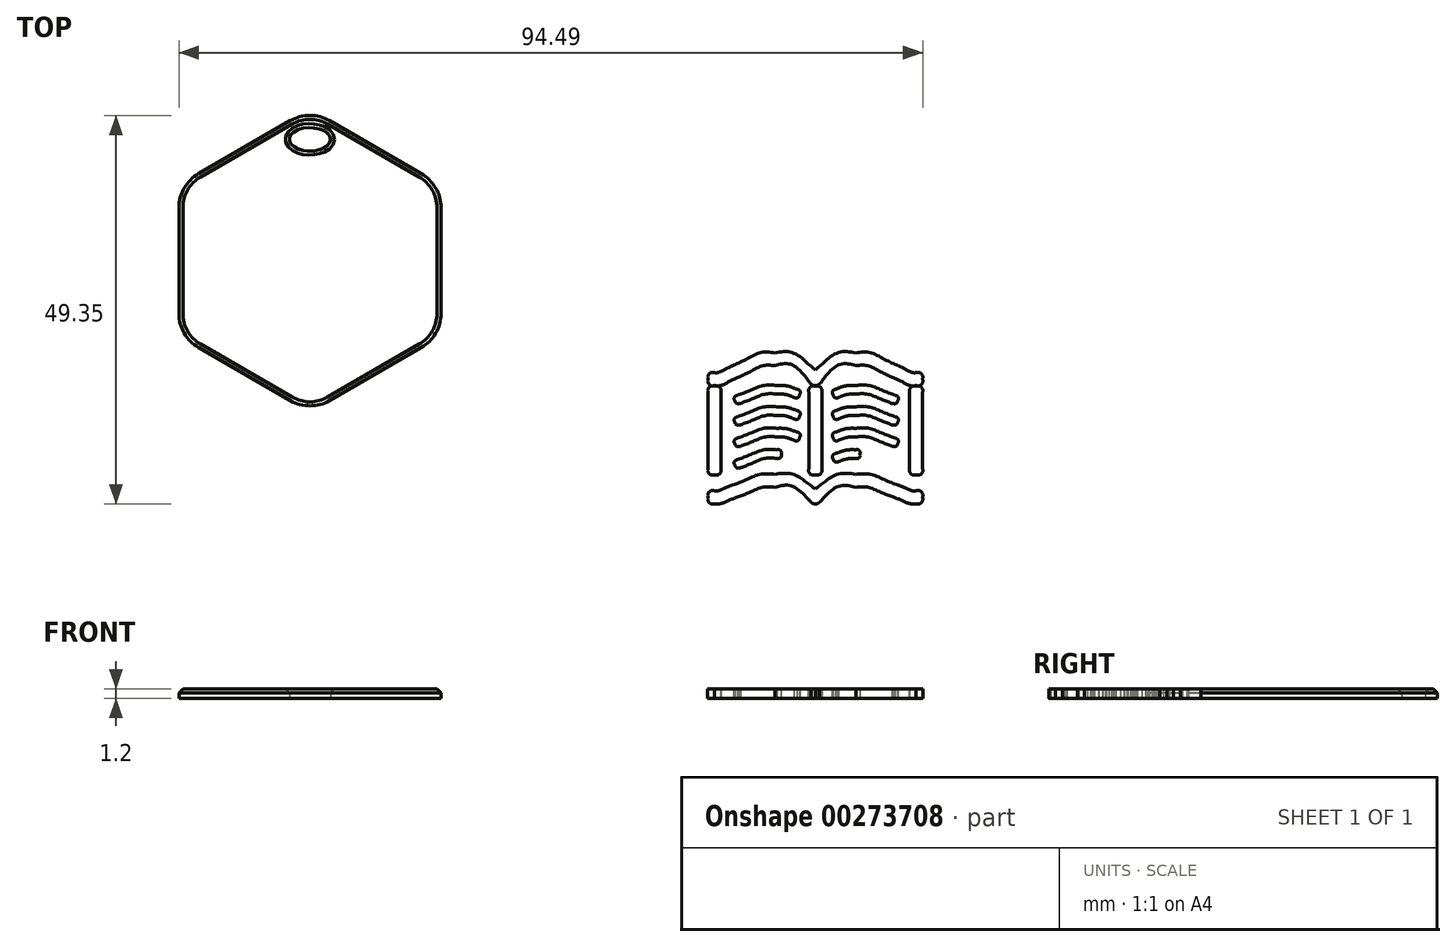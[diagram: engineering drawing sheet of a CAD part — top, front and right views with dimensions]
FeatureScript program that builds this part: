
annotation { "Feature Type Name" : "Feature", "Feature Type Description" : "" }
export const myFeature = defineFeature(function(context is Context, id is Id, definition is map)
    precondition{}
    {
        {
            var Q0;
            Q0=qCreatedBy(makeId("Top.planeOp"),FACE);
            var sketch = newSketch(context, id + "F0", { "sketchPlane" : qUnion([Q0])});
            skCircle(sketch, "E0.cCircle", {"center": v(0, 0) * mm, "radius": 16.64 * mm, "construction": true});
            skLineSegment(sketch, "E0.0", {"start": v(16.64, 6.72) * mm, "end": v(16.64, -6.72) * mm});
            skLineSegment(sketch, "E0.1", {"start": v(14.14, -11.05) * mm, "end": v(2.5, -17.77) * mm});
            skLineSegment(sketch, "E0.2", {"start": v(-2.5, -17.77) * mm, "end": v(-14.14, -11.05) * mm});
            skLineSegment(sketch, "E0.3", {"start": v(-16.64, -6.72) * mm, "end": v(-16.64, 6.72) * mm});
            skLineSegment(sketch, "E0.4", {"start": v(-14.14, 11.05) * mm, "end": v(-2.5, 17.77) * mm});
            skLineSegment(sketch, "E0.5", {"start": v(2.5, 17.77) * mm, "end": v(14.14, 11.05) * mm});
            skPoint(sketch, "E0.0.midPoint", {"position": v(16.64, 0) * mm});
            skPoint(sketch, "E1.visualSharp", {"position": v(-16.64, 9.6) * mm});
            skArc(sketch, "E1.filletArc", {"start": v(-14.14, 11.05) * mm, "mid": v(-15.97, 9.22) * mm, "end": v(-16.64, 6.72) * mm});
            skPoint(sketch, "E2.visualSharp", {"position": v(0, 19.22) * mm});
            skArc(sketch, "E2.filletArc", {"start": v(2.5, 17.77) * mm, "mid": v(0, 18.44) * mm, "end": v(-2.5, 17.77) * mm});
            skPoint(sketch, "E3.visualSharp", {"position": v(16.64, 9.6) * mm});
            skArc(sketch, "E3.filletArc", {"start": v(16.64, 6.72) * mm, "mid": v(15.97, 9.22) * mm, "end": v(14.14, 11.05) * mm});
            skPoint(sketch, "E4.visualSharp", {"position": v(16.64, -9.6) * mm});
            skArc(sketch, "E4.filletArc", {"start": v(14.14, -11.05) * mm, "mid": v(15.97, -9.22) * mm, "end": v(16.64, -6.72) * mm});
            skPoint(sketch, "E5.visualSharp", {"position": v(0, -19.22) * mm});
            skArc(sketch, "E5.filletArc", {"start": v(-2.5, -17.77) * mm, "mid": v(0, -18.44) * mm, "end": v(2.5, -17.77) * mm});
            skPoint(sketch, "E6.visualSharp", {"position": v(-16.64, -9.6) * mm});
            skArc(sketch, "E6.filletArc", {"start": v(-16.64, -6.72) * mm, "mid": v(-15.97, -9.22) * mm, "end": v(-14.14, -11.05) * mm});
            skPoint(sketch, "E7.visualSharp", {"position": v(-14.64, 8.45) * mm});
            skPoint(sketch, "E8.visualSharp", {"position": v(0, 16.9) * mm});
            skPoint(sketch, "E9.visualSharp", {"position": v(14.64, 8.45) * mm});
            skPoint(sketch, "E10.visualSharp", {"position": v(14.64, -8.45) * mm});
            skPoint(sketch, "E11.visualSharp", {"position": v(0, -16.9) * mm});
            skPoint(sketch, "E12.visualSharp", {"position": v(-14.64, -8.45) * mm});
            skEllipse(sketch, "E13", {"center": v(0, 15.41) * mm, "majorRadius": 2.6 * mm, "minorRadius": 1.5 * mm, "majorAxis": v(1, 0)});
            skFitSpline(sketch, "E14", {"points": [v(64.2, -15.87) * mm, v(64.07, -15.87) * mm, v(63.95, -15.84) * mm, v(63.84, -15.79) * mm]});
            skFitSpline(sketch, "E15", {"points": [v(63.84, -15.79) * mm, v(63.76, -15.75) * mm, v(63.68, -15.7) * mm, v(63.61, -15.63) * mm]});
            skFitSpline(sketch, "E16", {"points": [v(63.61, -15.63) * mm, v(63.6, -15.62) * mm, v(63.59, -15.6) * mm, v(63.58, -15.6) * mm]});
            skFitSpline(sketch, "E17", {"points": [v(63.58, -15.6) * mm, v(63.48, -15.5) * mm, v(61.46, -13.35) * mm, v(59.05, -13.35) * mm]});
            skFitSpline(sketch, "E18", {"points": [v(59.05, -13.35) * mm, v(57.55, -13.35) * mm, v(55.77, -14.18) * mm, v(54.34, -14.85) * mm]});
            skFitSpline(sketch, "E19", {"points": [v(54.34, -14.85) * mm, v(53.12, -15.42) * mm, v(52.16, -15.87) * mm, v(51.39, -15.87) * mm]});
            skFitSpline(sketch, "E20", {"points": [v(51.39, -15.87) * mm, v(50.93, -15.87) * mm, v(50.56, -15.5) * mm, v(50.56, -15.05) * mm]});
            skFitSpline(sketch, "E21", {"points": [v(50.56, -15.05) * mm, v(50.56, -14.6) * mm, v(50.93, -14.23) * mm, v(51.39, -14.23) * mm]});
            skFitSpline(sketch, "E22", {"points": [v(51.39, -14.23) * mm, v(51.8, -14.23) * mm, v(52.73, -13.79) * mm, v(53.64, -13.36) * mm]});
            skFitSpline(sketch, "E23", {"points": [v(53.64, -13.36) * mm, v(55.22, -12.62) * mm, v(57.18, -11.7) * mm, v(59.05, -11.7) * mm]});
            skFitSpline(sketch, "E24", {"points": [v(59.05, -11.7) * mm, v(61.35, -11.7) * mm, v(63.26, -13.08) * mm, v(64.2, -13.9) * mm]});
            skFitSpline(sketch, "E25", {"points": [v(64.2, -13.9) * mm, v(65.13, -13.08) * mm, v(67.04, -11.7) * mm, v(69.34, -11.7) * mm]});
            skFitSpline(sketch, "E26", {"points": [v(69.34, -11.7) * mm, v(71.2, -11.7) * mm, v(73.17, -12.62) * mm, v(74.75, -13.36) * mm]});
            skFitSpline(sketch, "E27", {"points": [v(74.75, -13.36) * mm, v(75.65, -13.79) * mm, v(76.59, -14.23) * mm, v(77, -14.23) * mm]});
            skFitSpline(sketch, "E28", {"points": [v(77, -14.23) * mm, v(77.45, -14.23) * mm, v(77.82, -14.6) * mm, v(77.82, -15.05) * mm]});
            skFitSpline(sketch, "E29", {"points": [v(77.82, -15.05) * mm, v(77.82, -15.5) * mm, v(77.45, -15.87) * mm, v(77, -15.87) * mm]});
            skFitSpline(sketch, "E30", {"points": [v(77, -15.87) * mm, v(76.22, -15.87) * mm, v(75.26, -15.42) * mm, v(74.05, -14.85) * mm]});
            skFitSpline(sketch, "E31", {"points": [v(74.05, -14.85) * mm, v(72.62, -14.18) * mm, v(70.84, -13.35) * mm, v(69.34, -13.35) * mm]});
            skFitSpline(sketch, "E32", {"points": [v(69.34, -13.35) * mm, v(66.91, -13.35) * mm, v(64.92, -15.48) * mm, v(64.8, -15.6) * mm]});
            skFitSpline(sketch, "E33", {"points": [v(64.8, -15.6) * mm, v(64.8, -15.6) * mm, v(64.79, -15.62) * mm, v(64.77, -15.63) * mm]});
            skFitSpline(sketch, "E34", {"points": [v(64.77, -15.63) * mm, v(64.7, -15.7) * mm, v(64.63, -15.75) * mm, v(64.55, -15.79) * mm]});
            skFitSpline(sketch, "E35", {"points": [v(64.55, -15.79) * mm, v(64.44, -15.84) * mm, v(64.3, -15.86) * mm, v(64.2, -15.87) * mm]});
            skFitSpline(sketch, "E36", {"points": [v(54.5, -26.34) * mm, v(54.28, -26.34) * mm, v(54.07, -26.2) * mm, v(53.99, -26) * mm]});
            skFitSpline(sketch, "E37", {"points": [v(53.99, -26) * mm, v(53.88, -25.7) * mm, v(54.02, -25.4) * mm, v(54.3, -25.28) * mm]});
            skFitSpline(sketch, "E38", {"points": [v(54.3, -25.28) * mm, v(55.94, -24.65) * mm, v(57.68, -24.03) * mm, v(59.31, -24.03) * mm]});
            skFitSpline(sketch, "E39", {"points": [v(59.31, -24.03) * mm, v(59.62, -24.03) * mm, v(59.86, -24.27) * mm, v(59.86, -24.57) * mm]});
            skFitSpline(sketch, "E40", {"points": [v(59.86, -24.57) * mm, v(59.86, -24.88) * mm, v(59.62, -25.12) * mm, v(59.31, -25.12) * mm]});
            skFitSpline(sketch, "E41", {"points": [v(59.31, -25.12) * mm, v(57.75, -25.12) * mm, v(55.91, -25.83) * mm, v(54.7, -26.3) * mm]});
            skFitSpline(sketch, "E42", {"points": [v(54.7, -26.3) * mm, v(54.63, -26.33) * mm, v(54.57, -26.34) * mm, v(54.5, -26.34) * mm]});
            skFitSpline(sketch, "E43", {"points": [v(66.97, -25.57) * mm, v(66.75, -25.57) * mm, v(66.54, -25.43) * mm, v(66.46, -25.21) * mm]});
            skFitSpline(sketch, "E44", {"points": [v(66.46, -25.21) * mm, v(66.35, -24.93) * mm, v(66.5, -24.61) * mm, v(66.78, -24.5) * mm]});
            skFitSpline(sketch, "E45", {"points": [v(66.78, -24.5) * mm, v(67.64, -24.19) * mm, v(68.5, -24.03) * mm, v(69.33, -24.03) * mm]});
            skFitSpline(sketch, "E46", {"points": [v(69.33, -24.03) * mm, v(69.63, -24.03) * mm, v(69.88, -24.27) * mm, v(69.88, -24.57) * mm]});
            skFitSpline(sketch, "E47", {"points": [v(69.88, -24.57) * mm, v(69.88, -24.88) * mm, v(69.63, -25.12) * mm, v(69.33, -25.12) * mm]});
            skFitSpline(sketch, "E48", {"points": [v(69.33, -25.12) * mm, v(68.63, -25.12) * mm, v(67.9, -25.26) * mm, v(67.16, -25.53) * mm]});
            skFitSpline(sketch, "E49", {"points": [v(67.16, -25.53) * mm, v(67.1, -25.56) * mm, v(67.04, -25.57) * mm, v(66.97, -25.57) * mm]});
            skFitSpline(sketch, "E50", {"points": [v(74.15, -23.62) * mm, v(74.08, -23.62) * mm, v(74.01, -23.6) * mm, v(73.95, -23.58) * mm]});
            skFitSpline(sketch, "E51", {"points": [v(73.95, -23.58) * mm, v(72.4, -22.98) * mm, v(70.78, -22.4) * mm, v(69.33, -22.4) * mm]});
            skFitSpline(sketch, "E52", {"points": [v(69.33, -22.4) * mm, v(68.63, -22.4) * mm, v(67.9, -22.54) * mm, v(67.16, -22.8) * mm]});
            skFitSpline(sketch, "E53", {"points": [v(67.16, -22.8) * mm, v(66.88, -22.92) * mm, v(66.57, -22.77) * mm, v(66.46, -22.49) * mm]});
            skFitSpline(sketch, "E54", {"points": [v(66.46, -22.49) * mm, v(66.35, -22.2) * mm, v(66.5, -21.89) * mm, v(66.78, -21.78) * mm]});
            skFitSpline(sketch, "E55", {"points": [v(66.78, -21.78) * mm, v(67.64, -21.46) * mm, v(68.5, -21.3) * mm, v(69.33, -21.3) * mm]});
            skFitSpline(sketch, "E56", {"points": [v(69.33, -21.3) * mm, v(70.97, -21.3) * mm, v(72.7, -21.92) * mm, v(74.34, -22.56) * mm]});
            skFitSpline(sketch, "E57", {"points": [v(74.34, -22.56) * mm, v(74.63, -22.67) * mm, v(74.77, -22.99) * mm, v(74.66, -23.27) * mm]});
            skFitSpline(sketch, "E58", {"points": [v(74.66, -23.27) * mm, v(74.57, -23.49) * mm, v(74.36, -23.62) * mm, v(74.15, -23.62) * mm]});
            skFitSpline(sketch, "E59", {"points": [v(54.5, -23.62) * mm, v(54.28, -23.62) * mm, v(54.07, -23.49) * mm, v(53.99, -23.27) * mm]});
            skFitSpline(sketch, "E60", {"points": [v(53.99, -23.27) * mm, v(53.88, -22.99) * mm, v(54.02, -22.67) * mm, v(54.3, -22.56) * mm]});
            skFitSpline(sketch, "E61", {"points": [v(54.3, -22.56) * mm, v(55.94, -21.92) * mm, v(57.67, -21.3) * mm, v(59.31, -21.3) * mm]});
            skFitSpline(sketch, "E62", {"points": [v(59.31, -21.3) * mm, v(60.15, -21.3) * mm, v(61, -21.46) * mm, v(61.86, -21.78) * mm]});
            skFitSpline(sketch, "E63", {"points": [v(61.86, -21.78) * mm, v(62.15, -21.89) * mm, v(62.3, -22.2) * mm, v(62.19, -22.49) * mm]});
            skFitSpline(sketch, "E64", {"points": [v(62.19, -22.49) * mm, v(62.08, -22.77) * mm, v(61.76, -22.91) * mm, v(61.48, -22.8) * mm]});
            skFitSpline(sketch, "E65", {"points": [v(61.48, -22.8) * mm, v(60.74, -22.54) * mm, v(60.02, -22.4) * mm, v(59.32, -22.4) * mm]});
            skFitSpline(sketch, "E66", {"points": [v(59.32, -22.4) * mm, v(57.87, -22.4) * mm, v(56.24, -22.98) * mm, v(54.7, -23.58) * mm]});
            skFitSpline(sketch, "E67", {"points": [v(54.7, -23.58) * mm, v(54.63, -23.6) * mm, v(54.57, -23.62) * mm, v(54.5, -23.62) * mm]});
            skFitSpline(sketch, "E68", {"points": [v(74.15, -20.9) * mm, v(74.08, -20.9) * mm, v(74.01, -20.88) * mm, v(73.95, -20.86) * mm]});
            skFitSpline(sketch, "E69", {"points": [v(73.95, -20.86) * mm, v(72.4, -20.26) * mm, v(70.78, -19.67) * mm, v(69.33, -19.67) * mm]});
            skFitSpline(sketch, "E70", {"points": [v(69.33, -19.67) * mm, v(68.63, -19.67) * mm, v(67.9, -19.81) * mm, v(67.16, -20.08) * mm]});
            skFitSpline(sketch, "E71", {"points": [v(67.16, -20.08) * mm, v(66.88, -20.2) * mm, v(66.57, -20.05) * mm, v(66.46, -19.76) * mm]});
            skFitSpline(sketch, "E72", {"points": [v(66.46, -19.76) * mm, v(66.35, -19.48) * mm, v(66.5, -19.16) * mm, v(66.78, -19.06) * mm]});
            skFitSpline(sketch, "E73", {"points": [v(66.78, -19.06) * mm, v(67.64, -18.74) * mm, v(68.5, -18.58) * mm, v(69.33, -18.58) * mm]});
            skFitSpline(sketch, "E74", {"points": [v(69.33, -18.58) * mm, v(70.97, -18.58) * mm, v(72.7, -19.2) * mm, v(74.34, -19.83) * mm]});
            skFitSpline(sketch, "E75", {"points": [v(74.34, -19.83) * mm, v(74.63, -19.94) * mm, v(74.77, -20.26) * mm, v(74.66, -20.54) * mm]});
            skFitSpline(sketch, "E76", {"points": [v(74.66, -20.54) * mm, v(74.57, -20.76) * mm, v(74.36, -20.9) * mm, v(74.15, -20.9) * mm]});
            skFitSpline(sketch, "E77", {"points": [v(54.5, -20.9) * mm, v(54.28, -20.9) * mm, v(54.07, -20.76) * mm, v(53.99, -20.54) * mm]});
            skFitSpline(sketch, "E78", {"points": [v(53.99, -20.54) * mm, v(53.88, -20.26) * mm, v(54.02, -19.94) * mm, v(54.3, -19.83) * mm]});
            skFitSpline(sketch, "E79", {"points": [v(54.3, -19.83) * mm, v(55.94, -19.2) * mm, v(57.68, -18.58) * mm, v(59.31, -18.58) * mm]});
            skFitSpline(sketch, "E80", {"points": [v(59.31, -18.58) * mm, v(60.15, -18.58) * mm, v(61, -18.74) * mm, v(61.86, -19.06) * mm]});
            skFitSpline(sketch, "E81", {"points": [v(61.86, -19.06) * mm, v(62.15, -19.16) * mm, v(62.3, -19.48) * mm, v(62.19, -19.76) * mm]});
            skFitSpline(sketch, "E82", {"points": [v(62.19, -19.76) * mm, v(62.08, -20.05) * mm, v(61.76, -20.2) * mm, v(61.48, -20.08) * mm]});
            skFitSpline(sketch, "E83", {"points": [v(61.48, -20.08) * mm, v(60.74, -19.81) * mm, v(60.02, -19.67) * mm, v(59.32, -19.67) * mm]});
            skFitSpline(sketch, "E84", {"points": [v(59.32, -19.67) * mm, v(57.87, -19.67) * mm, v(56.24, -20.26) * mm, v(54.7, -20.86) * mm]});
            skFitSpline(sketch, "E85", {"points": [v(54.7, -20.86) * mm, v(54.63, -20.88) * mm, v(54.57, -20.9) * mm, v(54.5, -20.9) * mm]});
            skFitSpline(sketch, "E86", {"points": [v(74.15, -18.17) * mm, v(74.08, -18.17) * mm, v(74.01, -18.16) * mm, v(73.95, -18.13) * mm]});
            skFitSpline(sketch, "E87", {"points": [v(73.95, -18.13) * mm, v(72.4, -17.53) * mm, v(70.78, -16.95) * mm, v(69.33, -16.95) * mm]});
            skFitSpline(sketch, "E88", {"points": [v(69.33, -16.95) * mm, v(68.63, -16.95) * mm, v(67.9, -17.09) * mm, v(67.16, -17.36) * mm]});
            skFitSpline(sketch, "E89", {"points": [v(67.16, -17.36) * mm, v(66.88, -17.46) * mm, v(66.57, -17.32) * mm, v(66.46, -17.04) * mm]});
            skFitSpline(sketch, "E90", {"points": [v(66.46, -17.04) * mm, v(66.35, -16.75) * mm, v(66.5, -16.44) * mm, v(66.78, -16.33) * mm]});
            skFitSpline(sketch, "E91", {"points": [v(66.78, -16.33) * mm, v(67.64, -16.01) * mm, v(68.5, -15.85) * mm, v(69.33, -15.85) * mm]});
            skFitSpline(sketch, "E92", {"points": [v(69.33, -15.85) * mm, v(70.97, -15.85) * mm, v(72.7, -16.47) * mm, v(74.34, -17.1) * mm]});
            skFitSpline(sketch, "E93", {"points": [v(74.34, -17.1) * mm, v(74.63, -17.22) * mm, v(74.77, -17.54) * mm, v(74.66, -17.82) * mm]});
            skFitSpline(sketch, "E94", {"points": [v(74.66, -17.82) * mm, v(74.57, -18.04) * mm, v(74.36, -18.17) * mm, v(74.15, -18.17) * mm]});
            skFitSpline(sketch, "E95", {"points": [v(54.5, -18.17) * mm, v(54.28, -18.17) * mm, v(54.07, -18.04) * mm, v(53.99, -17.82) * mm]});
            skFitSpline(sketch, "E96", {"points": [v(53.99, -17.82) * mm, v(53.88, -17.54) * mm, v(54.02, -17.22) * mm, v(54.3, -17.1) * mm]});
            skFitSpline(sketch, "E97", {"points": [v(54.3, -17.1) * mm, v(55.94, -16.47) * mm, v(57.68, -15.85) * mm, v(59.31, -15.85) * mm]});
            skFitSpline(sketch, "E98", {"points": [v(59.31, -15.85) * mm, v(60.15, -15.85) * mm, v(61, -16.01) * mm, v(61.86, -16.33) * mm]});
            skFitSpline(sketch, "E99", {"points": [v(61.86, -16.33) * mm, v(62.15, -16.44) * mm, v(62.3, -16.75) * mm, v(62.19, -17.04) * mm]});
            skFitSpline(sketch, "E100", {"points": [v(62.19, -17.04) * mm, v(62.08, -17.32) * mm, v(61.77, -17.46) * mm, v(61.48, -17.36) * mm]});
            skFitSpline(sketch, "E101", {"points": [v(61.48, -17.36) * mm, v(60.74, -17.09) * mm, v(60.01, -16.95) * mm, v(59.32, -16.95) * mm]});
            skFitSpline(sketch, "E102", {"points": [v(59.32, -16.95) * mm, v(57.87, -16.95) * mm, v(56.24, -17.53) * mm, v(54.7, -18.13) * mm]});
            skFitSpline(sketch, "E103", {"points": [v(54.7, -18.13) * mm, v(54.63, -18.16) * mm, v(54.57, -18.17) * mm, v(54.5, -18.17) * mm]});
            skFitSpline(sketch, "E104", {"points": [v(64.2, -30.88) * mm, v(64, -30.88) * mm, v(63.8, -30.8) * mm, v(63.64, -30.66) * mm]});
            skFitSpline(sketch, "E105", {"points": [v(63.64, -30.66) * mm, v(63.62, -30.64) * mm, v(61.55, -28.79) * mm, v(59.05, -28.79) * mm]});
            skFitSpline(sketch, "E106", {"points": [v(59.05, -28.79) * mm, v(57.52, -28.79) * mm, v(55.73, -29.48) * mm, v(54.28, -30.04) * mm]});
            skFitSpline(sketch, "E107", {"points": [v(54.28, -30.04) * mm, v(53.08, -30.5) * mm, v(52.13, -30.88) * mm, v(51.39, -30.88) * mm]});
            skFitSpline(sketch, "E108", {"points": [v(51.39, -30.88) * mm, v(50.93, -30.88) * mm, v(50.56, -30.5) * mm, v(50.56, -30.06) * mm]});
            skFitSpline(sketch, "E109", {"points": [v(50.56, -30.06) * mm, v(50.56, -29.6) * mm, v(50.93, -29.23) * mm, v(51.39, -29.23) * mm]});
            skFitSpline(sketch, "E110", {"points": [v(51.39, -29.23) * mm, v(51.83, -29.23) * mm, v(52.77, -28.87) * mm, v(53.69, -28.5) * mm]});
            skFitSpline(sketch, "E111", {"points": [v(53.69, -28.5) * mm, v(55.26, -27.9) * mm, v(57.21, -27.14) * mm, v(59.05, -27.14) * mm]});
            skFitSpline(sketch, "E112", {"points": [v(59.05, -27.14) * mm, v(61.36, -27.14) * mm, v(63.29, -28.33) * mm, v(64.2, -29) * mm]});
            skFitSpline(sketch, "E113", {"points": [v(64.2, -29) * mm, v(65.1, -28.33) * mm, v(67.03, -27.14) * mm, v(69.34, -27.14) * mm]});
            skFitSpline(sketch, "E114", {"points": [v(69.34, -27.14) * mm, v(71.17, -27.14) * mm, v(73.13, -27.9) * mm, v(74.7, -28.5) * mm]});
            skFitSpline(sketch, "E115", {"points": [v(74.7, -28.5) * mm, v(75.61, -28.87) * mm, v(76.56, -29.23) * mm, v(77, -29.23) * mm]});
            skFitSpline(sketch, "E116", {"points": [v(77, -29.23) * mm, v(77.45, -29.23) * mm, v(77.82, -29.6) * mm, v(77.82, -30.06) * mm]});
            skFitSpline(sketch, "E117", {"points": [v(77.82, -30.06) * mm, v(77.82, -30.5) * mm, v(77.45, -30.88) * mm, v(77, -30.88) * mm]});
            skFitSpline(sketch, "E118", {"points": [v(77, -30.88) * mm, v(76.25, -30.88) * mm, v(75.3, -30.5) * mm, v(74.1, -30.04) * mm]});
            skFitSpline(sketch, "E119", {"points": [v(74.1, -30.04) * mm, v(72.66, -29.48) * mm, v(70.87, -28.79) * mm, v(69.34, -28.79) * mm]});
            skFitSpline(sketch, "E120", {"points": [v(69.34, -28.79) * mm, v(66.87, -28.79) * mm, v(64.84, -30.58) * mm, v(64.75, -30.66) * mm]});
            skFitSpline(sketch, "E121", {"points": [v(64.75, -30.66) * mm, v(64.6, -30.8) * mm, v(64.4, -30.88) * mm, v(64.2, -30.88) * mm]});
            skFitSpline(sketch, "E122", {"points": [v(77, -27.21) * mm, v(76.55, -27.21) * mm, v(76.18, -26.85) * mm, v(76.18, -26.4) * mm]});
            skFitSpline(sketch, "E123", {"points": [v(76.18, -16.76) * mm, v(76.18, -16.31) * mm, v(76.55, -15.94) * mm, v(77, -15.94) * mm]});
            skFitSpline(sketch, "E124", {"points": [v(77, -15.94) * mm, v(77.45, -15.94) * mm, v(77.82, -16.31) * mm, v(77.82, -16.76) * mm]});
            skLineSegment(sketch, "E125", {"start": v(76.18, -26.4) * mm, "end": v(76.18, -16.76) * mm});
            skFitSpline(sketch, "E126", {"points": [v(77.82, -26.4) * mm, v(77.82, -26.85) * mm, v(77.46, -27.21) * mm, v(77, -27.21) * mm]});
            skFitSpline(sketch, "E127", {"points": [v(64.2, -27.21) * mm, v(63.74, -27.21) * mm, v(63.37, -26.85) * mm, v(63.37, -26.4) * mm]});
            skLineSegment(sketch, "E128", {"start": v(77.82, -16.76) * mm, "end": v(77.82, -26.4) * mm});
            skFitSpline(sketch, "E129", {"points": [v(63.37, -16.76) * mm, v(63.37, -16.31) * mm, v(63.74, -15.94) * mm, v(64.2, -15.94) * mm]});
            skFitSpline(sketch, "E130", {"points": [v(64.2, -15.94) * mm, v(64.65, -15.94) * mm, v(65.02, -16.31) * mm, v(65.02, -16.76) * mm]});
            skLineSegment(sketch, "E131", {"start": v(63.37, -26.4) * mm, "end": v(63.37, -16.76) * mm});
            skFitSpline(sketch, "E132", {"points": [v(65.02, -26.4) * mm, v(65.02, -26.85) * mm, v(64.65, -27.21) * mm, v(64.2, -27.21) * mm]});
            skFitSpline(sketch, "E133", {"points": [v(51.39, -27.21) * mm, v(50.93, -27.21) * mm, v(50.56, -26.85) * mm, v(50.56, -26.4) * mm]});
            skLineSegment(sketch, "E134", {"start": v(65.02, -16.76) * mm, "end": v(65.02, -26.4) * mm});
            skFitSpline(sketch, "E135", {"points": [v(50.56, -16.76) * mm, v(50.56, -16.31) * mm, v(50.93, -15.94) * mm, v(51.39, -15.94) * mm]});
            skFitSpline(sketch, "E136", {"points": [v(51.39, -15.94) * mm, v(51.84, -15.94) * mm, v(52.2, -16.31) * mm, v(52.2, -16.76) * mm]});
            skLineSegment(sketch, "E137", {"start": v(50.56, -26.4) * mm, "end": v(50.56, -16.76) * mm});
            skFitSpline(sketch, "E138", {"points": [v(52.2, -26.4) * mm, v(52.2, -26.85) * mm, v(51.84, -27.21) * mm, v(51.39, -27.21) * mm]});
            skLineSegment(sketch, "E139", {"start": v(52.2, -16.76) * mm, "end": v(52.2, -26.4) * mm});
            skSolve(sketch);
        }
        {
            var Q0;
            Q0=qSketchRegion(id+"F0",true);
            var Q1;
            Q1=makeQuery(id+"F0.imprint","IMPRINT",FACE,{"disambiguationData":[TD([[makeQuery(id+"F0.imprint","IMPRINT",EDGE,{"derivedFrom":sQuery(id+"F0.wireOp",EDGE,"9e54eab9-2333-4ba0-af71-57363ad4d06c")}),1.0]])]});
            var Q2;
            {var subQ5=sQuery(id+"F0.wireOp",EDGE,"b98c7cdd-8079-49cc-bf54-eea2d9e520bf");var subQ6=sQuery(id+"F0.wireOp",EDGE,"2e37fdde-fa08-406a-88b8-5b5253d86a45");var subQ7=makeQuery(id+"F0.imprint","INTERSECT",VERTEX,{"derivedFrom":[subQ6,subQ5]});Q2=makeQuery(id+"F0.imprint","IMPRINT",FACE,{"disambiguationData":[TD([[makeQuery(id+"F0.imprint","IMPRINT",EDGE,{"disambiguationData":[TD([[subQ7,1.0]])],"derivedFrom":subQ6}),-1.0]])]});}
            var Q3;
            {var subQ0=sQuery(id+"F0.wireOp",EDGE,"oH3uhxvT-U38n-sUFS-lbB8-VzE5z2EZjDcf.bottom");Q3=makeQuery(id+"F0.imprint","IMPRINT",FACE,{"disambiguationData":[TD([[makeQuery(id+"F0.imprint","IMPRINT",EDGE,{"derivedFrom":subQ0}),-1.0]])]});}
            var Q4;
            {var subQ1=sQuery(id+"F0.wireOp",EDGE,"oH3uhxvT-U38n-sUFS-lbB8-VzE5z2EZjDcf.top");Q4=makeQuery(id+"F0.imprint","IMPRINT",FACE,{"disambiguationData":[TD([[makeQuery(id+"F0.imprint","IMPRINT",EDGE,{"derivedFrom":subQ1}),1.0]])]});}
            var Q5;
            {var subQ7=sQuery(id+"F0.wireOp",EDGE,"2c25c595-052b-4228-92ce-aaaacbfd9761");var subQ8=sQuery(id+"F0.wireOp",EDGE,"95d9e6c1-34e6-48a4-96c1-f447036f3ee9");var subQ9=makeQuery(id+"F0.imprint","INTERSECT",VERTEX,{"derivedFrom":[subQ8,subQ7]});Q5=makeQuery(id+"F0.imprint","IMPRINT",FACE,{"disambiguationData":[TD([[makeQuery(id+"F0.imprint","IMPRINT",EDGE,{"disambiguationData":[TD([[subQ9,1.0]])],"derivedFrom":subQ8}),-1.0]])]});}
            var Q6;
            {var subQ1=sQuery(id+"F0.wireOp",EDGE,"66S6sztI-Wj7B-MLCr-koyH-eZ8carxLWydU.bottom");Q6=makeQuery(id+"F0.imprint","IMPRINT",FACE,{"disambiguationData":[TD([[makeQuery(id+"F0.imprint","IMPRINT",EDGE,{"derivedFrom":subQ1}),-1.0]])]});}
            var Q7;
            {var subQ9=sQuery(id+"F0.wireOp",EDGE,"300245b3-6fee-48c5-b711-db86c962e50a");Q7=makeQuery(id+"F0.imprint","IMPRINT",FACE,{"disambiguationData":[TD([[makeQuery(id+"F0.imprint","IMPRINT",EDGE,{"derivedFrom":subQ9}),1.0]])]});}
            extrude(context, id + "F1", {"entities" : qUnion([Q0, Q1, Q2, Q3, Q4, Q5, Q6, Q7]), "depth" : 1.2 * mm});
        }
        {
            var Q0;
            Q0=makeQuery(id+"F1.opExtrude","CAP_EDGE",EDGE,{"disambiguationData":[OSD([sQuery(id+"F0.wireOp",EDGE,"E0.2")])],"isStart":false});
            chamfer(context, id + "F2", {"entities" : qUnion([Q0]), "width" : 0.5 * mm, "tangentPropagation" : true});
        }
        {
            var Q0;
            Q0=makeQuery(id+"F1.opExtrude","CAP_EDGE",EDGE,{"disambiguationData":[OSD([sQuery(id+"F0.wireOp",EDGE,"E13")])],"isStart":false});
            chamfer(context, id + "F3", {"entities" : qUnion([Q0]), "width" : 0.5 * mm, "tangentPropagation" : true});
        }
    });
